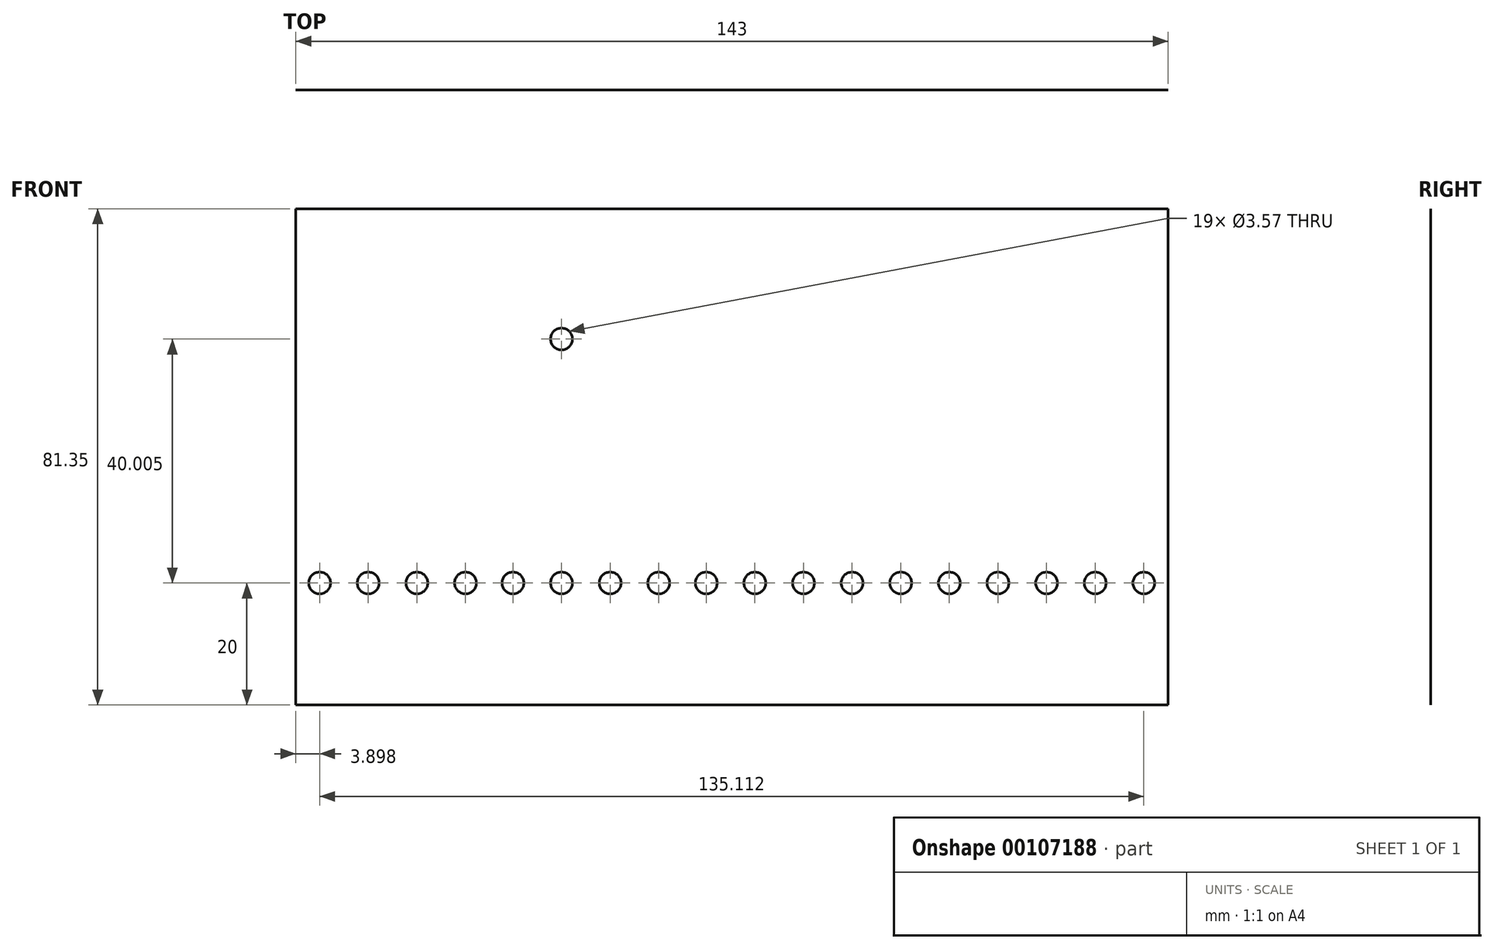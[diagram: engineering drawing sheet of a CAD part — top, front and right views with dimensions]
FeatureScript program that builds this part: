
annotation { "Feature Type Name" : "Feature", "Feature Type Description" : "" }
export const myFeature = defineFeature(function(context is Context, id is Id, definition is map)
    precondition{}
    {
        {
            var Q0;
            Q0=qCreatedBy(makeId("Front.planeOp"),FACE);
            var sketch = newSketch(context, id + "F0", { "sketchPlane" : qUnion([Q0])});
            skPoint(sketch, "E0.middle", {"position": v(0, 0) * mm});
            skCircle(sketch, "E1", {"center": v(0, 0) * mm, "radius": 1.79 * mm});
            skCircle(sketch, "E2.1.0.0", {"center": v(7.97, 0) * mm, "radius": 1.79 * mm});
            skCircle(sketch, "E2.2.0.0", {"center": v(15.94, 0) * mm, "radius": 1.79 * mm});
            skCircle(sketch, "E2.3.0.0", {"center": v(23.91, 0) * mm, "radius": 1.79 * mm});
            skCircle(sketch, "E2.4.0.0", {"center": v(31.88, 0) * mm, "radius": 1.79 * mm});
            skCircle(sketch, "E2.5.0.0", {"center": v(39.85, 0) * mm, "radius": 1.79 * mm});
            skCircle(sketch, "E2.6.0.0", {"center": v(47.82, 0) * mm, "radius": 1.79 * mm});
            skCircle(sketch, "E2.7.0.0", {"center": v(55.8, 0) * mm, "radius": 1.79 * mm});
            skCircle(sketch, "E2.8.0.0", {"center": v(63.76, 0) * mm, "radius": 1.79 * mm});
            skCircle(sketch, "E2.9.0.0", {"center": v(71.73, 0) * mm, "radius": 1.79 * mm});
            skLineSegment(sketch, "E2.direction1", {"start": v(0, 0) * mm, "end": v(7.97, 0) * mm, "construction": true});
            skLineSegment(sketch, "E3", {"start": v(75.72, 61.35) * mm, "end": v(-3.71, 61.35) * mm});
            skLineSegment(sketch, "E4", {"start": v(75.72, -20) * mm, "end": v(-3.9, -20) * mm});
            skCircle(sketch, "E5.MirrorC", {"center": v(-7.8, 0) * mm, "radius": 1.79 * mm});
            skCircle(sketch, "E6.MirrorC", {"center": v(-15.76, 0) * mm, "radius": 1.79 * mm});
            skCircle(sketch, "E7.MirrorC", {"center": v(-23.73, 0) * mm, "radius": 1.79 * mm});
            skCircle(sketch, "E8.MirrorC", {"center": v(-31.7, 0) * mm, "radius": 1.79 * mm});
            skLineSegment(sketch, "E9.bottom", {"start": v(-3.9, -20) * mm, "end": v(-35.59, -20) * mm});
            skLineSegment(sketch, "E9.top", {"start": v(-3.71, 61.35) * mm, "end": v(-35.4, 61.35) * mm});
            skCircle(sketch, "E10.MirrorC", {"center": v(-63.38, 0) * mm, "radius": 1.79 * mm});
            skCircle(sketch, "E11.MirrorC", {"center": v(-47.44, 0) * mm, "radius": 1.79 * mm});
            skCircle(sketch, "E12.MirrorC", {"center": v(-55.41, 0) * mm, "radius": 1.79 * mm});
            skCircle(sketch, "E13.MirrorC", {"center": v(-39.47, 0) * mm, "radius": 1.79 * mm});
            skLineSegment(sketch, "E14", {"start": v(-67.28, -20) * mm, "end": v(-67.28, 61.35) * mm});
            skPoint(sketch, "E14.startSnap0", {"position": v(-67.28, 5.4) * mm});
            skPoint(sketch, "E14.endSnap0", {"position": v(-67.28, 29.6) * mm});
            skLineSegment(sketch, "E15", {"start": v(-67.28, 61.35) * mm, "end": v(-35.4, 61.35) * mm});
            skLineSegment(sketch, "E16", {"start": v(-35.59, -20) * mm, "end": v(-67.28, -20) * mm});
            skCircle(sketch, "E17", {"center": v(-23.73, 40) * mm, "radius": 1.79 * mm});
            skLineSegment(sketch, "E18", {"start": v(75.72, -20) * mm, "end": v(75.72, 61.35) * mm});
            skSolve(sketch);
        }
        {
            var Q0;
            Q0=makeQuery(id+"F0.imprint","IMPRINT",FACE,{"disambiguationData":[TD([[makeQuery(id+"F0.imprint","IMPRINT",EDGE,{"derivedFrom":sQuery(id+"F0.wireOp",EDGE,"E1")}),-1.0]])]});
            extrude(context, id + "F1", {"entities" : qUnion([Q0]), "depth" : 1 / 203.2 * mm});
        }
    });
